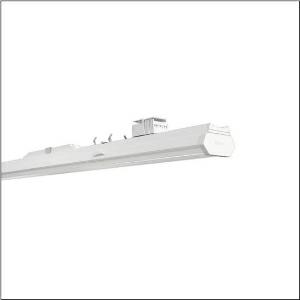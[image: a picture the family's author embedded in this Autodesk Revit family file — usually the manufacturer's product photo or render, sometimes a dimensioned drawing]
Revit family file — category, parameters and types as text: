
# Revit family: licross_r__11_protected_ho_51tp12dn4exl3s4_c748
name_source: partatom
category: Lighting Fixtures
units: mm (PartAtom-declared; Revit-internal decimal feet)

## family parameters
Cut with Voids When Loaded = No
Host = Face
Light Source = No
Part Type = Normal
Room Calculation Point = No
Round Connector Dimension = Use Diameter
Shared = No

## types (1)
- --- (1 x LED, 14070 lm, 89.8 W, 4000K)
    Apparent Load = 90 VA
    CIE Flux Codes = 70 91 97 98 100
    Color Rendering = 80
    Color Temperature = 4000K
    Default Elevation = 1800 mm
    Description = Licross® 11 Protected HO, luminaire insert, of sheet steel, galvanised, coil coated, white, length: 1.500mm, width: 90mm, height: 101mm, LED rated luminous flux: 14.070lm, light colour: 840, control gear: DALI 2, control gear: ECG DALI, with plug, 6-pole, with phase selection, for trunking rail, 9 or 11-core, mains connection: 220..240V, AC/DC, 0/50..60Hz, halogen-free wiring, for emergency light function, converter,control gear: single battery element, battery: LiFeP04, 9Ah, primary optical cover: cover, of PMMA, light emission: direct with ceiling illumination distribution, primary light characteristic: symmetric, protection rating (complete): IP64, insulation class (complete): insulation class I (protective earthing), certification: CE, UKCA, protection symbol: D if used in an environment with conductive dust loads with corresponding accessories, permissible ambient temperature for indoor applications: +5..+30°C, standard: EN 60598-2-22, corresponds to IFS (International Featured Standards) requirements for safety and quality in the food industry, reducing of maximum allowable ambient temperature of 5°C with ceiling mounting, LABS conformity tested according to VDMA 24364:2018-05, packaging unit: 1 piece
    Height = 92 mm
    Lamp = 1 x LED
    Lamp Light Flux = 14070 lm
    Lamp Power = 89.8 W
    Lamp count = 1
    Length = 1500 mm
    Luminous efficacy = 157 lm/W
    Manufacturer = Siteco
    ModVariant = No
    Model = 51TP12DN4EXL3S4
    Mounting Place = Ceiling
    Mounting Type = Pendant
    Number of Poles = 1
    OnlyDefault = Yes
    Power Factor = 1
    Product Name = Licross® 11 Protected HO
    Product group = luminaire insert
    ProductGroupID = 902
    Protection Class = Protection class I
    Protection Degree = IP 64
    RLX_Detail_Level = 1
    RlxData = <blob elided: 24945 chars, md5=21c2680c>
    Socket = socket
    Standby Power = 0 W
    System Light Flux = 14070 lm
    System Power = 90 W
    Type Comments = : AC-mode, luminous flux: 100 % | dim-lin: 254 | 485 mA
    Type Image = l_1256148.jpg
    URL = http://relux.com
    VarID = @adj_115695
    Voltage = 0 V
    Weight = 0.00 kg
    Width = 88 mm

## geometry (parser evidence)
native form markers: Blend x4, Sweep x12
no freeform markers — native parametric forms only
